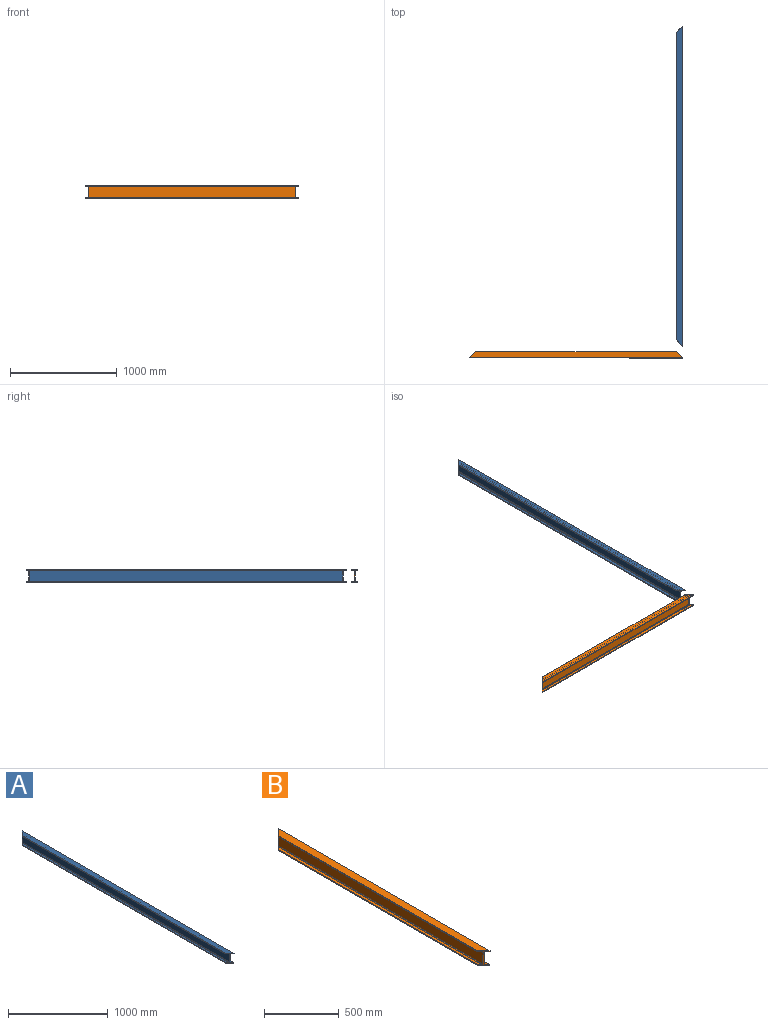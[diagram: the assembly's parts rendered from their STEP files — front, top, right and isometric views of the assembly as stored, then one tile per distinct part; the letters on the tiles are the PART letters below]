
ASSEMBLY  parts=2 mates=1
PART A: 18 faces, bbox 60.1x3000x120 mm
  f0: plane 2999.81x8mm, normal (1,0,0), area 23998.5mm2, adj f1,f15,f16,f17
  f1: plane 2999.81x21.99mm, normal (0,0,1), area 65493.5mm2, adj f0,f2,f16,f17
  f2: cylinder r=5mm len=2955.83mm, axis (0,-1,0), area 23165mm2, adj f1,f3,f16,f17
  f3: plane 2945.99x94mm, normal (1,0,0), area 276917.6mm2, adj f2,f4,f16,f17
  f4: cylinder r=5mm len=2956mm, axis (0,-1,0), area 23166.3mm2, adj f3,f5,f16,f17
  f5: plane 3000x22mm, normal (0,0,-1), area 65516mm2, adj f4,f6,f16,f17
  f6: plane 3000x8mm, normal (1,0,0), area 23998.2mm2, adj f5,f7,f16,f17
  f7: plane 3000x60mm, normal (0,0,1), area 176400mm2, adj f6,f8,f16,f17
  f8: plane 2880x8mm, normal (-1,0,0), area 23040mm2, adj f7,f9,f16,f17
  f9: plane 2924x22mm, normal (0,0,-1), area 63844mm2, adj f8,f10,f16,f17
  f10: cylinder r=5mm len=2933.99mm, axis (0,-1,0), area 23015mm2, adj f9,f11,f16,f17
  f11: plane 2933.99x94mm, normal (-1,0,0), area 275789.4mm2, adj f10,f12,f16,f17
  f12: cylinder r=5mm len=2933.83mm, axis (0,-1,0), area 23013.7mm2, adj f11,f13,f16,f17
  f13: plane 2923.83x21.91mm, normal (0,0,1), area 63589.6mm2, adj f12,f14,f16,f17
  f14: plane 2880x8mm, normal (-1,0,0.01), area 23039.2mm2, adj f13,f15,f16,f17
  f15: plane 2999.8x60mm, normal (0,0,-1), area 176388mm2, adj f0,f14,f16,f17
  f16: plane 120x60.1mm, normal (-0.71,-0.71,0), area 2269.9mm2, adj f0,f1,f2,f3,f4,f5,f6,f7
  f17: plane 120x60.1mm, normal (-0.71,0.71,0), area 2269.9mm2, adj f0,f1,f2,f3,f4,f5,f6,f7
PART B: 18 faces, bbox 60.1x2000x120 mm
  f0: plane 1999.81x8mm, normal (1,0,0), area 15998.5mm2, adj f1,f15,f16,f17
  f1: plane 1999.81x21.99mm, normal (0,0,1), area 43499.7mm2, adj f0,f2,f16,f17
  f2: cylinder r=5mm len=1955.83mm, axis (0,-1,0), area 15311mm2, adj f1,f3,f16,f17
  f3: plane 1945.99x94mm, normal (1,0,0), area 182917mm2, adj f2,f4,f16,f17
  f4: cylinder r=5mm len=1956mm, axis (0,-1,0), area 15312.4mm2, adj f3,f5,f16,f17
  f5: plane 2000x22mm, normal (0,0,-1), area 43516mm2, adj f4,f6,f16,f17
  f6: plane 2000x8mm, normal (1,0,0), area 15998.8mm2, adj f5,f7,f16,f17
  f7: plane 2000x60mm, normal (0,0,1), area 116400mm2, adj f6,f8,f16,f17
  f8: plane 1880x8mm, normal (-1,0,0), area 15040mm2, adj f7,f9,f16,f17
  f9: plane 1924x22mm, normal (0,0,-1), area 41844mm2, adj f8,f10,f16,f17
  f10: cylinder r=5mm len=1933.99mm, axis (0,-1,0), area 15161mm2, adj f9,f11,f16,f17
  f11: plane 1933.99x94mm, normal (-1,0,0), area 181788.9mm2, adj f10,f12,f16,f17
  f12: cylinder r=5mm len=1933.83mm, axis (0,-1,0), area 15159.7mm2, adj f11,f13,f16,f17
  f13: plane 1923.83x21.91mm, normal (0,0,1), area 41676.6mm2, adj f12,f14,f16,f17
  f14: plane 1880x8mm, normal (-1,0,0.01), area 15039.2mm2, adj f13,f15,f16,f17
  f15: plane 1999.8x60mm, normal (0,0,-1), area 116388mm2, adj f0,f14,f16,f17
  f16: plane 120x60.1mm, normal (-0.71,-0.71,0), area 2269.9mm2, adj f0,f1,f2,f3,f4,f5,f6,f7
  f17: plane 120x60.1mm, normal (-0.71,0.71,0), area 2269.9mm2, adj f0,f1,f2,f3,f4,f5,f6,f7
PLACE A rot(axis=(0,0,-1),0deg) t=(-468,389.85,55.87)mm
PLACE B rot(axis=(0,0,-1),90deg) t=(-2437.95,309.9,55.87)mm
MATE planar A.f7 <-> B.f7  axis (0,0,1) through (-497.95,449.85,115.87)mm
